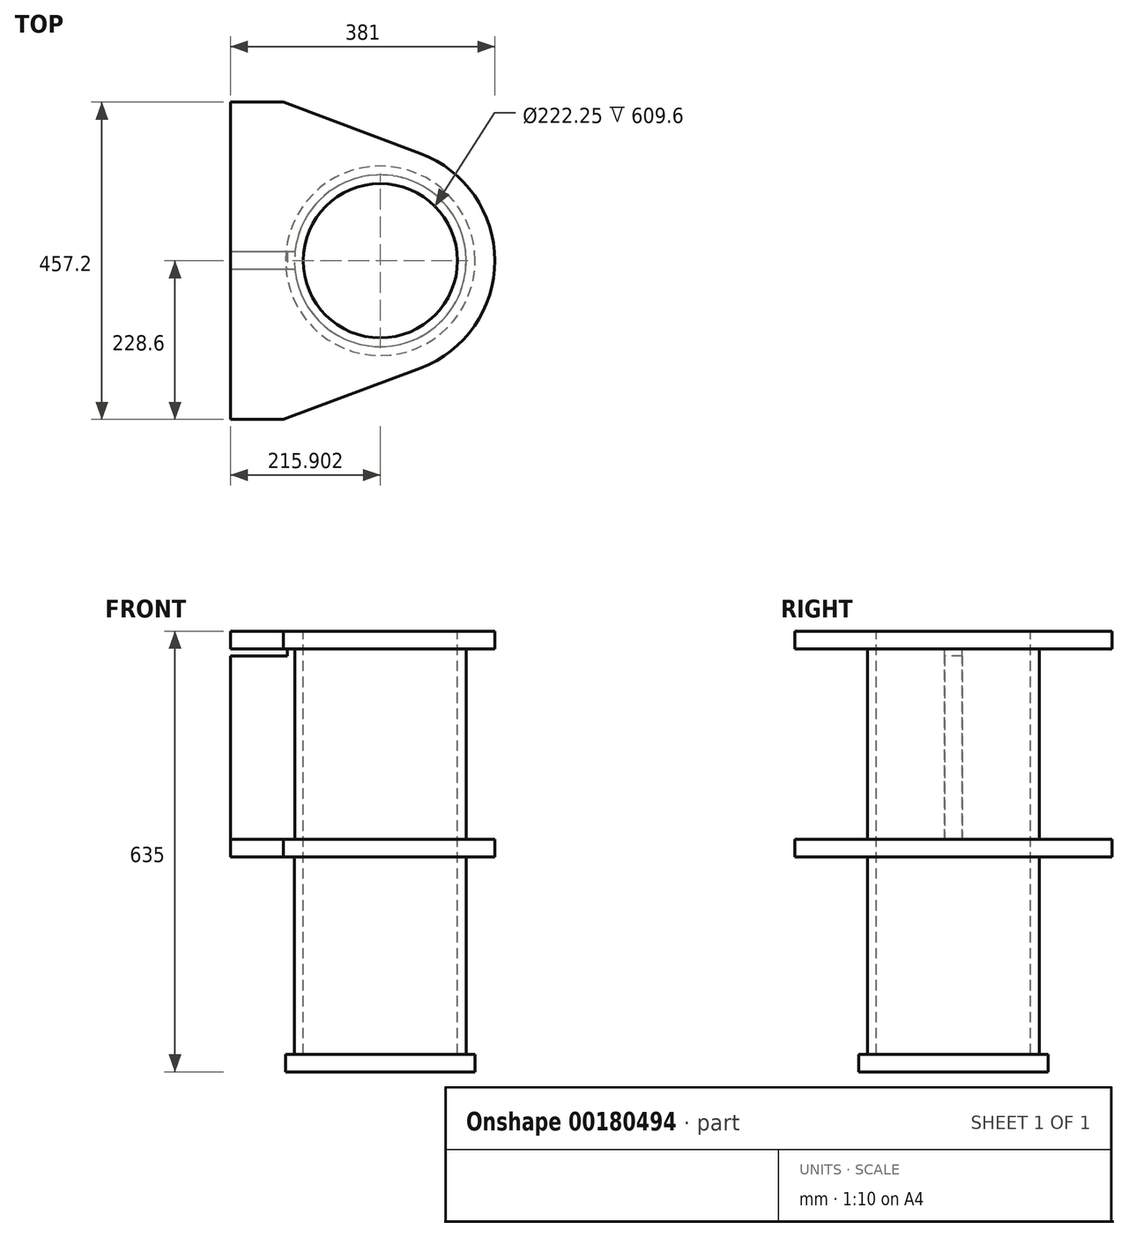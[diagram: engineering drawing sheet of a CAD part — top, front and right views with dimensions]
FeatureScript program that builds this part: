
annotation { "Feature Type Name" : "Feature", "Feature Type Description" : "" }
export const myFeature = defineFeature(function(context is Context, id is Id, definition is map)
    precondition{}
    {
        {
            var Q0;
            Q0=qCreatedBy(makeId("Top.planeOp"),FACE);
            var sketch = newSketch(context, id + "F0", { "sketchPlane" : qUnion([Q0])});
            skCircle(sketch, "E0", {"center": v(93.66, 0) * mm, "radius": 123.83 * mm});
            skArc(sketch, "E1", {"start": v(258.76, 0) * mm, "mid": v(229.34, 94.07) * mm, "end": v(151.55, 154.62) * mm});
            skLineSegment(sketch, "E2", {"start": v(93.66, 0) * mm, "end": v(-122.24, 0) * mm, "construction": true});
            skLineSegment(sketch, "E3", {"start": v(-122.24, 0) * mm, "end": v(-122.24, 228.6) * mm});
            skLineSegment(sketch, "E4", {"start": v(-122.24, 228.6) * mm, "end": v(-46.04, 228.6) * mm});
            skLineSegment(sketch, "E5", {"start": v(-46.04, 228.6) * mm, "end": v(151.55, 154.62) * mm});
            skLineSegment(sketch, "E6", {"start": v(93.66, 0) * mm, "end": v(258.76, 0) * mm, "construction": true});
            skArc(sketch, "E7.MirrorCS", {"start": v(258.76, 0) * mm, "mid": v(229.34, -94.07) * mm, "end": v(151.55, -154.62) * mm});
            skLineSegment(sketch, "E8.MirrorCS", {"start": v(-46.04, -228.6) * mm, "end": v(151.55, -154.62) * mm});
            skLineSegment(sketch, "E9.MirrorCS", {"start": v(-122.24, 0) * mm, "end": v(-122.24, -228.6) * mm});
            skLineSegment(sketch, "E10.MirrorCS", {"start": v(-122.24, -228.6) * mm, "end": v(-46.04, -228.6) * mm});
            skLineSegment(sketch, "E11", {"start": v(0, 494.92) * mm, "end": v(0, -494.92) * mm, "construction": true});
            skPoint(sketch, "E12", {"position": v(0, 0) * mm});
            skSolve(sketch);
        }
        {
            var Q0;
            Q0 = qSketchRegion(id + "F0", true);
            extrude(context, id + "F1", {"entities" : qUnion([Q0]), "oppositeDirection" : true, "depth" : 25.4 * mm});
        }
        {
            var Q0;
            Q0=qCreatedBy(makeId("Top.planeOp"),FACE);
            cPlane(context, id + "F2", {"entities" : qUnion([Q0]), "cplaneType" : CPlaneType.OFFSET, "offset" : 325.63 * mm, "oppositeDirection" : true, "width" : 152.4 * mm, "height" : 152.4 * mm});
        }
        {
            var Q0;
            Q0=qCreatedBy(id+"F2.planeOp",FACE);
            var sketch = newSketch(context, id + "F3", { "sketchPlane" : qUnion([Q0])});
            skArc(sketch, "E13.0.0", {"start": v(151.55, -154.62) * mm, "mid": v(258.76, 0) * mm, "end": v(151.55, 154.62) * mm});
            skLineSegment(sketch, "E13.0.1", {"start": v(151.55, 154.62) * mm, "end": v(-46.04, 228.6) * mm});
            skLineSegment(sketch, "E13.0.2", {"start": v(-46.04, 228.6) * mm, "end": v(-122.24, 228.6) * mm});
            skLineSegment(sketch, "E13.0.3", {"start": v(-122.24, 228.6) * mm, "end": v(-122.24, -228.6) * mm});
            skLineSegment(sketch, "E13.0.4", {"start": v(-122.24, -228.6) * mm, "end": v(-46.04, -228.6) * mm});
            skLineSegment(sketch, "E13.0.5", {"start": v(-46.04, -228.6) * mm, "end": v(151.55, -154.62) * mm});
            skCircle(sketch, "E14.0", {"center": v(93.66, 0) * mm, "radius": 123.83 * mm});
            skSolve(sketch);
        }
        {
            var Q0;
            Q0 = qSketchRegion(id + "F3", true);
            extrude(context, id + "F4", {"entities" : qUnion([Q0]), "depth" : 25.4 * mm});
        }
        {
            var Q0;
            Q0=makeQuery(id+"F1.opExtrude","CAP_FACE",FACE,{"disambiguationData":[OSD([sQuery(id+"F0.wireOp",EDGE,"E0"),sQuery(id+"F0.wireOp",EDGE,"E1"),sQuery(id+"F0.wireOp",EDGE,"E3"),sQuery(id+"F0.wireOp",EDGE,"E4"),sQuery(id+"F0.wireOp",EDGE,"E5"),sQuery(id+"F0.wireOp",EDGE,"E7.MirrorCS"),sQuery(id+"F0.wireOp",EDGE,"E8.MirrorCS"),sQuery(id+"F0.wireOp",EDGE,"E9.MirrorCS"),sQuery(id+"F0.wireOp",EDGE,"E10.MirrorCS")])],"isStart":true});
            var sketch = newSketch(context, id + "F5", { "sketchPlane" : qUnion([Q0])});
            skCircle(sketch, "E15.0", {"center": v(93.66, 0) * mm, "radius": 123.83 * mm});
            skCircle(sketch, "E16", {"center": v(93.66, 0) * mm, "radius": 111.13 * mm});
            skSolve(sketch);
        }
        {
            var Q0;
            Q0 = qSketchRegion(id + "F5", true);
            extrude(context, id + "F6", {"entities" : qUnion([Q0]), "operationType" : NewBodyOperationType.ADD, "oppositeDirection" : true, "depth" : 609.6 * mm});
        }
        {
            var Q0;
            Q0=makeQuery(id+"F6.opExtrude","CAP_FACE",FACE,{"disambiguationData":[OSD([sQuery(id+"F5.wireOp",EDGE,"E15.0"),sQuery(id+"F5.wireOp",EDGE,"E16")])],"isStart":false});
            var sketch = newSketch(context, id + "F7", { "sketchPlane" : qUnion([Q0])});
            skCircle(sketch, "E17", {"center": v(93.66, 0) * mm, "radius": 136.53 * mm});
            skSolve(sketch);
        }
        {
            var Q0;
            Q0 = qSketchRegion(id + "F7", true);
            extrude(context, id + "F8", {"entities" : qUnion([Q0]), "operationType" : NewBodyOperationType.ADD, "depth" : 25.4 * mm});
        }
        {
            var Q0;
            Q0=makeQuery(id+"F1.opExtrude","SWEPT_FACE",FACE,{"disambiguationData":[OSD([sQuery(id+"F0.wireOp",EDGE,"E3"),sQuery(id+"F0.wireOp",EDGE,"E9.MirrorCS")])]});
            var sketch = newSketch(context, id + "F9", { "sketchPlane" : qUnion([Q0])});
            skLineSegment(sketch, "E18.bottom", {"start": v(-12.7, -25.4) * mm, "end": v(12.7, -25.4) * mm});
            skLineSegment(sketch, "E18.top", {"start": v(-12.7, -300.23) * mm, "end": v(12.7, -300.23) * mm});
            skLineSegment(sketch, "E18.left", {"start": v(-12.7, -25.4) * mm, "end": v(-12.7, -300.23) * mm});
            skLineSegment(sketch, "E18.right", {"start": v(12.7, -25.4) * mm, "end": v(12.7, -300.23) * mm});
            skLineSegment(sketch, "E19", {"start": v(0, 0) * mm, "end": v(0, -25.4) * mm, "construction": true});
            skSolve(sketch);
        }
        {
            var Q0;
            Q0 = qSketchRegion(id + "F9", true);
            var Q1;
            Q1=makeQuery(id+"F6.boolean.opBoolean","SPLIT",FACE,{"disambiguationData":[TD([makeQuery(id+"F4.opExtrude","CAP_FACE",FACE,{"disambiguationData":[OSD([sQuery(id+"F3.wireOp",EDGE,"E13.0.0"),sQuery(id+"F3.wireOp",EDGE,"E13.0.1"),sQuery(id+"F3.wireOp",EDGE,"E13.0.2"),sQuery(id+"F3.wireOp",EDGE,"E13.0.3"),sQuery(id+"F3.wireOp",EDGE,"E13.0.4"),sQuery(id+"F3.wireOp",EDGE,"E13.0.5"),sQuery(id+"F3.wireOp",EDGE,"E14.0")])],"isStart":false})])],"derivedFrom":makeQuery(id+"F6.opExtrude","SWEPT_FACE",FACE,{"disambiguationData":[OSD([sQuery(id+"F5.wireOp",EDGE,"E15.0")])]})});
            extrude(context, id + "F10", {"entities" : qUnion([Q0]), "operationType" : NewBodyOperationType.ADD, "endBound" : BoundingType.UP_TO_SURFACE, "oppositeDirection" : true, "endBoundEntityFace" : qUnion([Q1]), "depth" : 25.4 * mm});
        }
        {
            var Q0;
            Q0=qCreatedBy(makeId("Front.planeOp"),FACE);
            var sketch = newSketch(context, id + "F11", { "sketchPlane" : qUnion([Q0])});
            skLineSegment(sketch, "E20.bottom", {"start": v(-122.24, -25.4) * mm, "end": v(-40.2, -25.4) * mm});
            skLineSegment(sketch, "E20.top", {"start": v(-122.24, -35.56) * mm, "end": v(-40.2, -35.56) * mm});
            skLineSegment(sketch, "E20.left", {"start": v(-122.24, -25.4) * mm, "end": v(-122.24, -35.56) * mm});
            skLineSegment(sketch, "E20.right", {"start": v(-40.2, -25.4) * mm, "end": v(-40.2, -35.56) * mm});
            skSolve(sketch);
        }
        {
            var Q0;
            Q0 = qSketchRegion(id + "F11", true);
            extrude(context, id + "F12", {"entities" : qUnion([Q0]), "operationType" : NewBodyOperationType.REMOVE, "endBound" : BoundingType.THROUGH_ALL, "oppositeDirection" : true, "depth" : 25.4 * mm, "hasSecondDirection" : true, "secondDirectionBound" : SecondDirectionBoundingType.THROUGH_ALL, "secondDirectionOppositeDirection" : false, "secondDirectionDepth" : 25.4 * mm});
        }
    });
